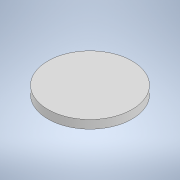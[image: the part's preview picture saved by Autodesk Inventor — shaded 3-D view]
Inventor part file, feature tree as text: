
AUTODESK INVENTOR PART (.ipt)
format: ipt  version: 2020.1 (Build 241239000, 239)  size: 89,088 bytes
history: native  units: mm
features: extrude x1, sketch x1
ambient origin geometry x8: Origin, YZ Plane, XZ Plane, XY Plane, X Axis, Y Axis, Z Axis, Center Point
bodies: Solid1 (feature_tree)
feature tree (2):
  extrude  "Extrusion1"  [1 undecoded]
  sketch  "Sketch1"  dims[d0=10.0mm d1=0.0mm]
note: 1 required parameter value undecoded (feature->parameter linkage not recoverable at this tier; creation-order binding heuristic only, values carry confidence <= 0.55)
